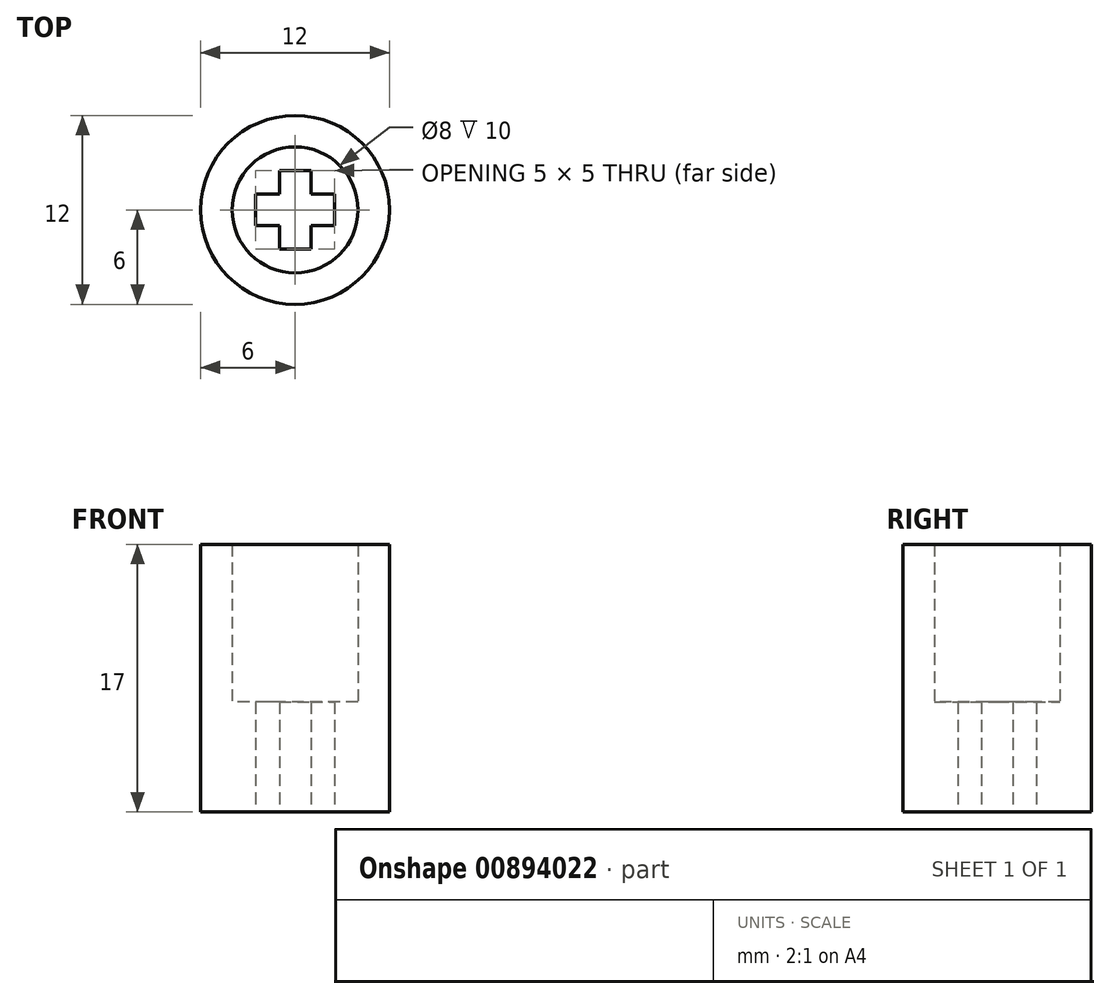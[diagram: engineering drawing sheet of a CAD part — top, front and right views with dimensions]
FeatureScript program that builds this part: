
annotation { "Feature Type Name" : "Feature", "Feature Type Description" : "" }
export const myFeature = defineFeature(function(context is Context, id is Id, definition is map)
    precondition{}
    {
        {
            var Q0;
            Q0=qCreatedBy(makeId("Top.planeOp"),FACE);
            var sketch = newSketch(context, id + "F0", { "sketchPlane" : qUnion([Q0])});
            skCircle(sketch, "E0", {"center": v(0, 0) * mm, "radius": 6 * mm});
            skCircle(sketch, "E1", {"center": v(0, 0) * mm, "radius": 4 * mm});
            skLineSegment(sketch, "E2", {"start": v(0, 2.5) * mm, "end": v(-1, 2.5) * mm});
            skLineSegment(sketch, "E3", {"start": v(-1, 2.5) * mm, "end": v(-1, 1) * mm});
            skLineSegment(sketch, "E4", {"start": v(-1, 1) * mm, "end": v(-2.5, 1) * mm});
            skLineSegment(sketch, "E5", {"start": v(-2.5, 1) * mm, "end": v(-2.5, 0) * mm});
            skLineSegment(sketch, "E6.MirrorCS", {"start": v(-2.5, -1) * mm, "end": v(-2.5, 0) * mm});
            skLineSegment(sketch, "E7.MirrorCS", {"start": v(-1, -1) * mm, "end": v(-2.5, -1) * mm});
            skLineSegment(sketch, "E8.MirrorCS", {"start": v(-1, -2.5) * mm, "end": v(-1, -1) * mm});
            skLineSegment(sketch, "E9.MirrorCS", {"start": v(0, -2.5) * mm, "end": v(-1, -2.5) * mm});
            skLineSegment(sketch, "E10.MirrorCS", {"start": v(0, -2.5) * mm, "end": v(1, -2.5) * mm});
            skLineSegment(sketch, "E11.MirrorCS", {"start": v(1, -2.5) * mm, "end": v(1, -1) * mm});
            skLineSegment(sketch, "E12.MirrorCS", {"start": v(1, -1) * mm, "end": v(2.5, -1) * mm});
            skLineSegment(sketch, "E13.MirrorCS", {"start": v(2.5, -1) * mm, "end": v(2.5, 0) * mm});
            skLineSegment(sketch, "E14.MirrorCS", {"start": v(1, 1) * mm, "end": v(2.5, 1) * mm});
            skLineSegment(sketch, "E15.MirrorCS", {"start": v(1, 2.5) * mm, "end": v(1, 1) * mm});
            skLineSegment(sketch, "E16.MirrorCS", {"start": v(0, 2.5) * mm, "end": v(1, 2.5) * mm});
            skLineSegment(sketch, "E17", {"start": v(2.5, 1) * mm, "end": v(2.5, 0) * mm});
            skSolve(sketch);
        }
        {
            var Q0;
            Q0=makeQuery(id+"F0.imprint","IMPRINT",FACE,{"disambiguationData":[TD([[makeQuery(id+"F0.imprint","IMPRINT",EDGE,{"derivedFrom":sQuery(id+"F0.wireOp",EDGE,"E1")}),1.0]])]});
            var Q1;
            Q1=makeQuery(id+"F0.imprint","IMPRINT",FACE,{"disambiguationData":[TD([[makeQuery(id+"F0.imprint","IMPRINT",EDGE,{"derivedFrom":sQuery(id+"F0.wireOp",EDGE,"E0")}),1.0]])]});
            extrude(context, id + "F1", {"entities" : qUnion([Q0, Q1]), "depth" : 7 * mm, "offsetDistance" : 25 * mm});
        }
        {
            var Q0;
            Q0=makeQuery(id+"F0.imprint","IMPRINT",FACE,{"disambiguationData":[TD([[makeQuery(id+"F0.imprint","IMPRINT",EDGE,{"derivedFrom":sQuery(id+"F0.wireOp",EDGE,"E0")}),1.0]])]});
            extrude(context, id + "F2", {"entities" : qUnion([Q0]), "operationType" : NewBodyOperationType.ADD, "depth" : 17 * mm, "offsetDistance" : 25 * mm});
        }
    });
